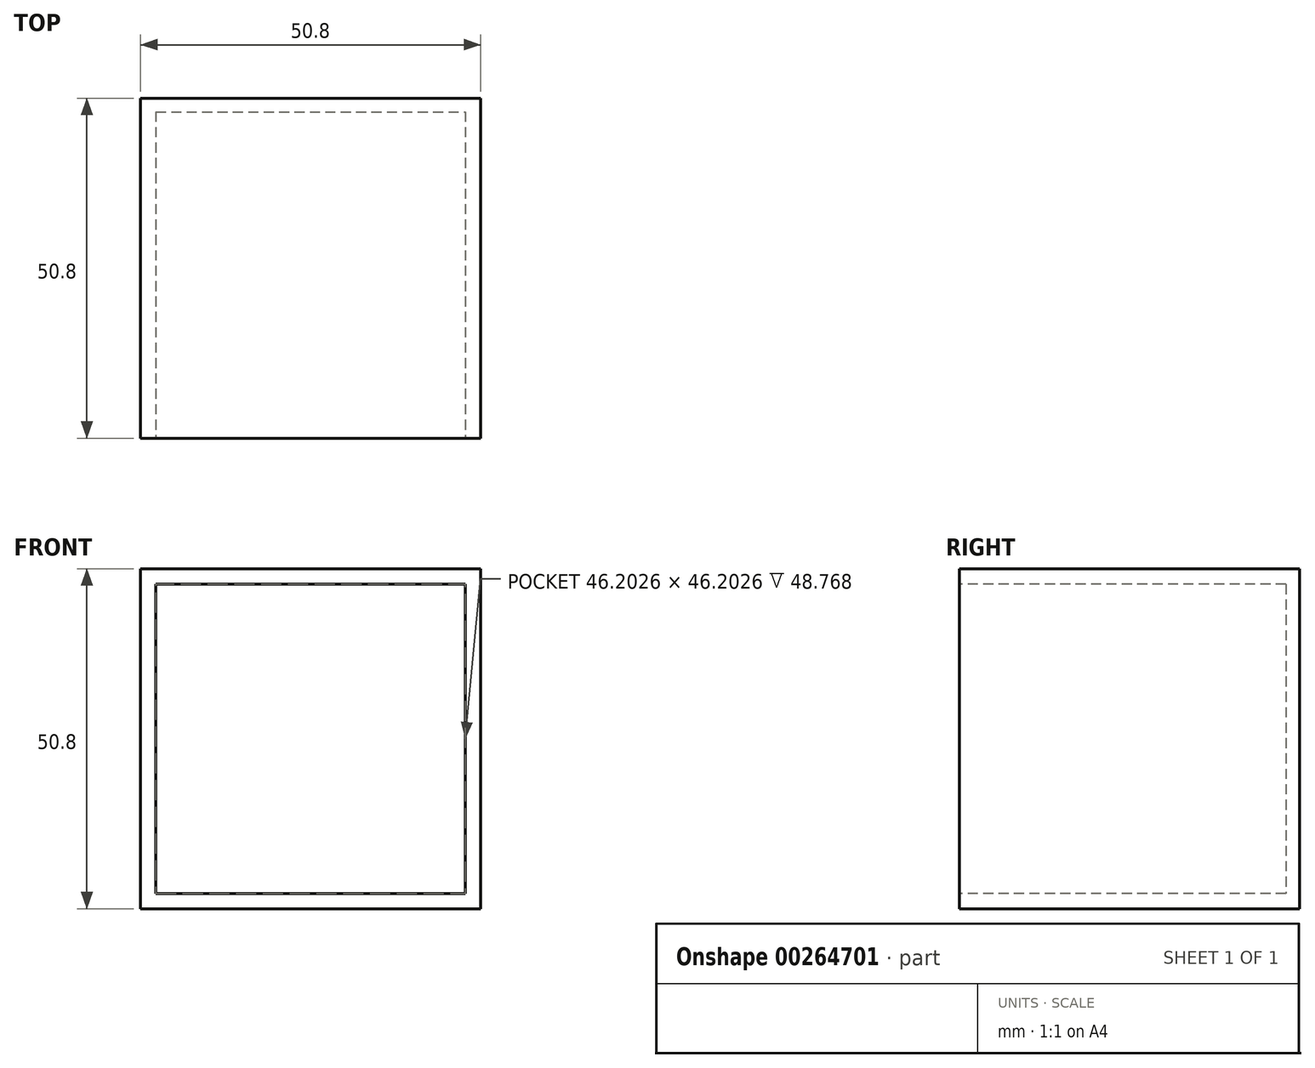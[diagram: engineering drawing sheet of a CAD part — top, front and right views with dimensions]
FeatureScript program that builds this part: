
annotation { "Feature Type Name" : "Feature", "Feature Type Description" : "" }
export const myFeature = defineFeature(function(context is Context, id is Id, definition is map)
    precondition{}
    {
        {
            var Q0;
            Q0=qCreatedBy(makeId("Front.planeOp"),FACE);
            var sketch = newSketch(context, id + "F0", { "sketchPlane" : qUnion([Q0])});
            skLineSegment(sketch, "E0.bottom", {"start": v(0, 0) * mm, "end": v(-50.8, 0) * mm});
            skLineSegment(sketch, "E0.top", {"start": v(0, 50.8) * mm, "end": v(-50.8, 50.8) * mm});
            skLineSegment(sketch, "E0.left", {"start": v(0, 0) * mm, "end": v(0, 50.8) * mm});
            skLineSegment(sketch, "E0.right", {"start": v(-50.8, 0) * mm, "end": v(-50.8, 50.8) * mm});
            skSolve(sketch);
        }
        {
            var Q0;
            Q0 = qSketchRegion(id + "F0", true);
            extrude(context, id + "F1", {"entities" : qUnion([Q0]), "depth" : 50.8 * mm});
        }
        {
            var Q0;
            Q0=makeQuery(id+"F1.opExtrude","CAP_FACE",FACE,{"disambiguationData":[OSD([sQuery(id+"F0.wireOp",EDGE,"E0.bottom"),sQuery(id+"F0.wireOp",EDGE,"E0.top"),sQuery(id+"F0.wireOp",EDGE,"E0.left"),sQuery(id+"F0.wireOp",EDGE,"E0.right")])],"isStart":false});
            var sketch = newSketch(context, id + "F2", { "sketchPlane" : qUnion([Q0])});
            skLineSegment(sketch, "E1.bottom", {"start": v(-48.89, 48.87) * mm, "end": v(-1.72, 48.87) * mm});
            skLineSegment(sketch, "E1.top", {"start": v(-48.89, 1.9) * mm, "end": v(-1.72, 1.9) * mm});
            skLineSegment(sketch, "E1.left", {"start": v(-48.89, 48.87) * mm, "end": v(-48.89, 1.9) * mm});
            skLineSegment(sketch, "E1.right", {"start": v(-1.72, 48.87) * mm, "end": v(-1.72, 1.9) * mm});
            skSolve(sketch);
        }
        {
            var Q0;
            Q0=makeQuery(id+"F2.imprint","IMPRINT",FACE,{"disambiguationData":[TD([[makeQuery(id+"F2.imprint","IMPRINT",EDGE,{"derivedFrom":sQuery(id+"F2.wireOp",EDGE,"E1.bottom")}),1.0]])]});
            extrude(context, id + "F3", {"entities" : qUnion([Q0]), "operationType" : NewBodyOperationType.ADD, "oppositeDirection" : true, "depth" : 49.53 * mm});
        }
        {
            var Q0;
            Q0=makeQuery(id+"F1.opExtrude","CAP_FACE",FACE,{"disambiguationData":[OSD([sQuery(id+"F0.wireOp",EDGE,"E0.bottom"),sQuery(id+"F0.wireOp",EDGE,"E0.top"),sQuery(id+"F0.wireOp",EDGE,"E0.left"),sQuery(id+"F0.wireOp",EDGE,"E0.right")])],"isStart":false});
            var sketch = newSketch(context, id + "F4", { "sketchPlane" : qUnion([Q0])});
            skLineSegment(sketch, "E2.bottom", {"start": v(-48.5, 48.5) * mm, "end": v(-2.3, 48.5) * mm});
            skLineSegment(sketch, "E2.top", {"start": v(-48.5, 2.3) * mm, "end": v(-2.3, 2.3) * mm});
            skLineSegment(sketch, "E2.left", {"start": v(-48.5, 48.5) * mm, "end": v(-48.5, 2.3) * mm});
            skLineSegment(sketch, "E2.right", {"start": v(-2.3, 48.5) * mm, "end": v(-2.3, 2.3) * mm});
            skSolve(sketch);
        }
        {
            var Q0;
            Q0=makeQuery(id+"F4.imprint","IMPRINT",FACE,{"disambiguationData":[TD([[makeQuery(id+"F4.imprint","IMPRINT",EDGE,{"derivedFrom":sQuery(id+"F4.wireOp",EDGE,"E2.bottom")}),-1.0]])]});
            extrude(context, id + "F5", {"entities" : qUnion([Q0]), "operationType" : NewBodyOperationType.REMOVE, "oppositeDirection" : true, "depth" : 48.77 * mm});
        }
    });
